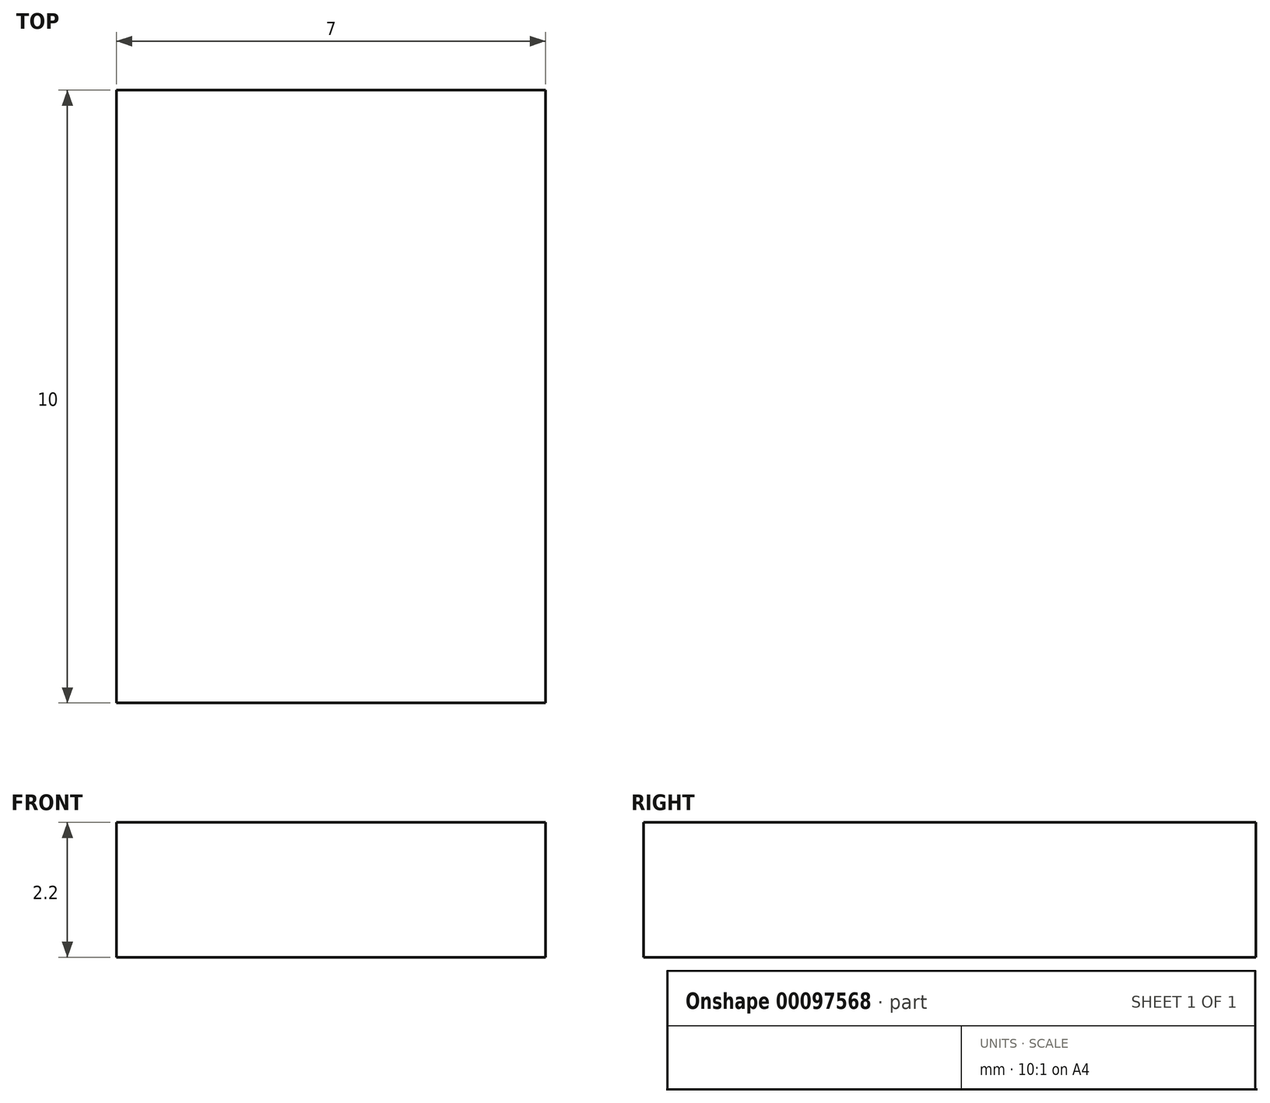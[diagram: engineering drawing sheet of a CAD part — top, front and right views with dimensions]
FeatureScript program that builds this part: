
annotation { "Feature Type Name" : "Feature", "Feature Type Description" : "" }
export const myFeature = defineFeature(function(context is Context, id is Id, definition is map)
    precondition{}
    {
        {
            var Q0;
            Q0=qCreatedBy(makeId("Top.planeOp"),FACE);
            var sketch = newSketch(context, id + "F0", { "sketchPlane" : qUnion([Q0])});
            skLineSegment(sketch, "E0.bottom", {"start": v(3.5, 5) * mm, "end": v(-3.5, 5) * mm});
            skLineSegment(sketch, "E0.top", {"start": v(3.5, -5) * mm, "end": v(-3.5, -5) * mm});
            skLineSegment(sketch, "E0.left", {"start": v(3.5, 5) * mm, "end": v(3.5, -5) * mm});
            skLineSegment(sketch, "E0.right", {"start": v(-3.5, 5) * mm, "end": v(-3.5, -5) * mm});
            skPoint(sketch, "E0.middle", {"position": v(0, 0) * mm});
            skSolve(sketch);
        }
        {
            var Q0;
            Q0=makeQuery(id+"F0.imprint","IMPRINT",FACE,{"disambiguationData":[TD([[makeQuery(id+"F0.imprint","IMPRINT",EDGE,{"derivedFrom":sQuery(id+"F0.wireOp",EDGE,"E0.bottom")}),1.0]])]});
            extrude(context, id + "F1", {"entities" : qUnion([Q0]), "depth" : 2.2 * mm});
        }
    });
